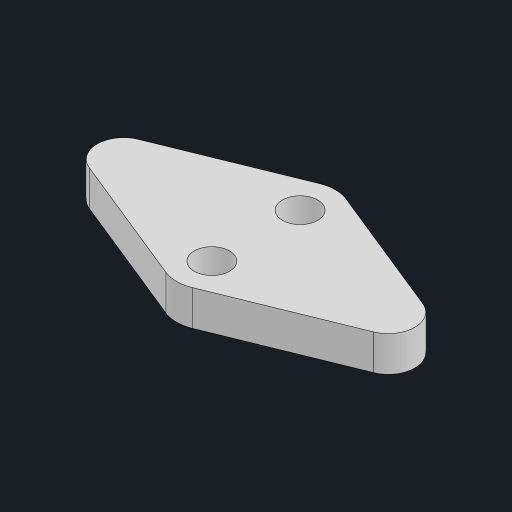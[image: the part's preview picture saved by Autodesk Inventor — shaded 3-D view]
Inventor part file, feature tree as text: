
AUTODESK INVENTOR PART (.ipt)
format: ipt  version: 2023 (Build 270158000, 158)  size: 107,520 bytes
history: native  units: mm
features: sketch x2, other x1, extrude x1, hole x1
ambient origin geometry x8: Origin, YZ Plane, XZ Plane, XY Plane, X Axis, Y Axis, Z Axis, Center Point
bodies: Body1 (feature_tree)
feature tree (5):
  other  "ソリッド1"
  extrude  "押し出し1"  Depth=5.0mm
  hole  "穴1"  [1 undecoded]
  sketch  "スケッチ1"
  sketch  "スケッチ2"
note: 1 required parameter value undecoded (feature->parameter linkage not recoverable at this tier; creation-order binding heuristic only, values carry confidence <= 0.55)
